# Revit family: 5ffedfa8_6e3b_414a_a20e_75c25b320b79
name_source: partatom
category: Plumbing Fixtures
revit_build: Autodesk Revit 2015 (Build: 20140903_1530(x64)
units: mm (PartAtom-declared; Revit-internal decimal feet)

## types (1)
- Default
    BIMobject category = Taps & Mixers
    BIMobject category code = sanitary-taps-mixers
    BIMobject main category = Sanitary
    BIMobject main category code = sanitary
    BOSUseNativeGeometries = 1
    Brand url = http://www.hansgrohe-int.com
    Design country = Germany
    Edition number = 1
    GTIN code = https://4059625196977
    IFC Classification = Sanitary Terminal
    Installation instructions = https://www.hansgrohe-usa.com
    Manufacturer country = Germany
    Manufacturer name = hansgrohe
    Masterformat 2014 Code = 22 41 39
    Masterformat 2014 Description = Residential Faucets, Supplies, and Trim
    NBS Reference Code = 31-75
    NBS Reference Description = Sanitary Accessories
    OmniClass Code = 23-31 11 00
    OmniClass Description = Faucets
    Product Guid = 60569394-8f63-4b88-a2df-8f5e589e87fa
    Product SKU = 04774670
    Product data url = https://bimobject.com
    Product family = Joleena
    Product group = Faucets
    Product name = 04774670 Joleena 3-hole basin mixer 100 with pop-up waste set
    Product url = https://www.hansgrohe-usa.com
    QR code = http://bimobject.com
    Technical description = https://www.hansgrohe-usa.com
    UNSPSC Code = 301815
    Uniclass 1.4 Code = L725111
    Uniclass 1.4 Description = Mixer taps
    Uniclass 2.0 Code = PR-31-75
    Uniclass 2.0 Description = Sanitary Accessories
    Uniclass 2015 Code = Pr_40_20_87_09
    Uniclass 2015 Name = Bath taps
    Uniformat II Code = D2010
    Uniformat II Description = Plumbing Fixtures

## geometry (parser evidence)
native form markers: Sweep x2
no freeform markers — native parametric forms only
